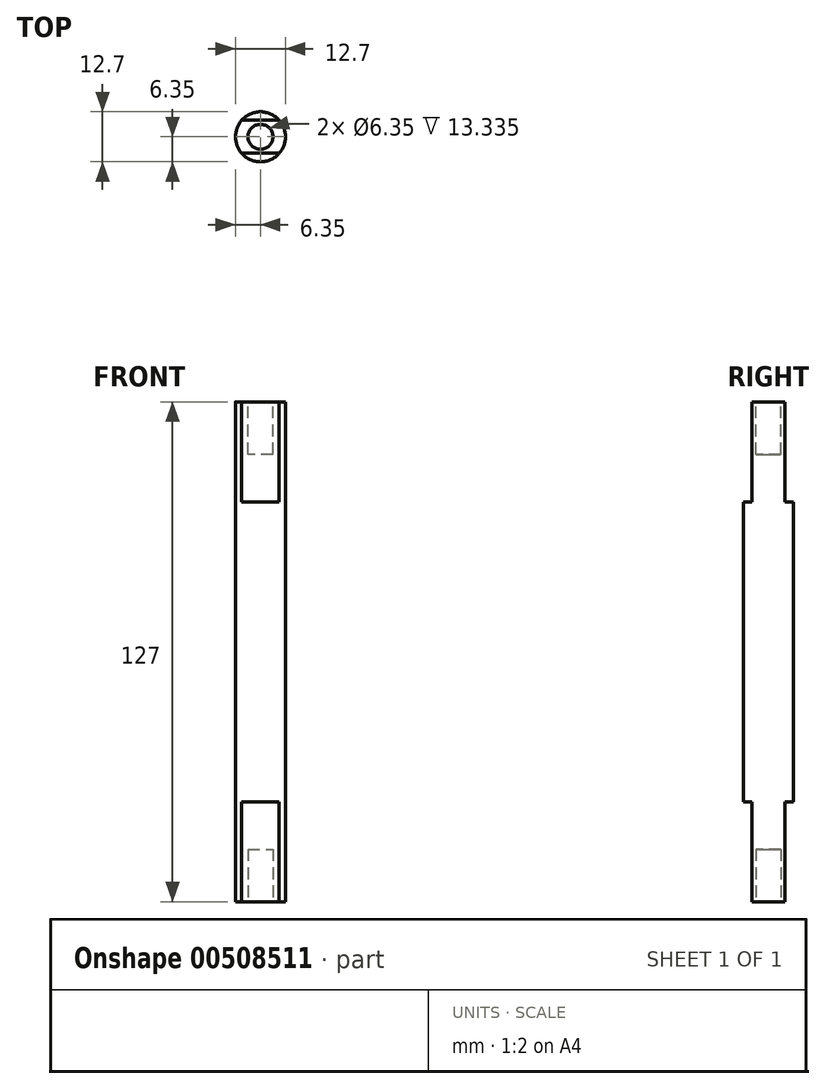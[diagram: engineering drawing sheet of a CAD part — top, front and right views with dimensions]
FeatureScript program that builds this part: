
annotation { "Feature Type Name" : "Feature", "Feature Type Description" : "" }
export const myFeature = defineFeature(function(context is Context, id is Id, definition is map)
    precondition{}
    {
        {
            var Q0;
            Q0=qCreatedBy(makeId("Top.planeOp"),FACE);
            var sketch = newSketch(context, id + "F0", { "sketchPlane" : qUnion([Q0])});
            skCircle(sketch, "E0", {"center": v(0, 0) * mm, "radius": 6.35 * mm});
            skSolve(sketch);
        }
        {
            var Q0;
            Q0=makeQuery(id+"F0.imprint","IMPRINT",FACE,{"disambiguationData":[TD([[makeQuery(id+"F0.imprint","IMPRINT",EDGE,{"derivedFrom":sQuery(id+"F0.wireOp",EDGE,"E0")}),1.0]])]});
            extrude(context, id + "F1", {"entities" : qUnion([Q0]), "depth" : 127 * mm, "offsetDistance" : 25.4 * mm});
        }
        {
            var Q0;
            Q0=makeQuery(id+"F1.opExtrude","CAP_FACE",FACE,{"disambiguationData":[OSD([sQuery(id+"F0.wireOp",EDGE,"E0")])],"isStart":true});
            var sketch = newSketch(context, id + "F2", { "sketchPlane" : qUnion([Q0])});
            skCircle(sketch, "E1", {"center": v(0, 0) * mm, "radius": 3.18 * mm});
            skSolve(sketch);
        }
        {
            var Q0;
            Q0=makeQuery(id+"F2.imprint","IMPRINT",FACE,{"disambiguationData":[TD([[makeQuery(id+"F2.imprint","IMPRINT",EDGE,{"derivedFrom":sQuery(id+"F2.wireOp",EDGE,"E1")}),1.0]])]});
            extrude(context, id + "F3", {"entities" : qUnion([Q0]), "operationType" : NewBodyOperationType.REMOVE, "oppositeDirection" : true, "depth" : 13.33 * mm, "offsetDistance" : 25.4 * mm});
        }
        {
            var Q0;
            Q0=makeQuery(id+"F1.opExtrude","CAP_FACE",FACE,{"disambiguationData":[OSD([sQuery(id+"F0.wireOp",EDGE,"E0")])],"isStart":false});
            var sketch = newSketch(context, id + "F4", { "sketchPlane" : qUnion([Q0])});
            skCircle(sketch, "E2", {"center": v(0, 0) * mm, "radius": 3.18 * mm});
            skSolve(sketch);
        }
        {
            var Q0;
            Q0=makeQuery(id+"F4.imprint","IMPRINT",FACE,{"disambiguationData":[TD([[makeQuery(id+"F4.imprint","IMPRINT",EDGE,{"derivedFrom":sQuery(id+"F4.wireOp",EDGE,"E2")}),1.0]])]});
            extrude(context, id + "F5", {"entities" : qUnion([Q0]), "operationType" : NewBodyOperationType.REMOVE, "oppositeDirection" : true, "depth" : 13.33 * mm, "offsetDistance" : 25.4 * mm});
        }
        {
            var Q0;
            Q0=makeQuery(id+"F1.opExtrude","CAP_FACE",FACE,{"disambiguationData":[OSD([sQuery(id+"F0.wireOp",EDGE,"E0")])],"isStart":true});
            var sketch = newSketch(context, id + "F6", { "sketchPlane" : qUnion([Q0])});
            skLineSegment(sketch, "E3.bottom", {"start": v(4.77, 4.2) * mm, "end": v(-4.77, 4.2) * mm});
            skLineSegment(sketch, "E3.top", {"start": v(4.77, -4.2) * mm, "end": v(-4.77, -4.2) * mm});
            skSolve(sketch);
        }
        {
            var Q0;
            {var subQ0=sQuery(id+"F6.wireOp",EDGE,"E3.bottom");Q0=makeQuery(id+"F6.imprint","IMPRINT",FACE,{"disambiguationData":[TD([[makeQuery(id+"F6.imprint","IMPRINT",EDGE,{"derivedFrom":subQ0}),-1.0]])]});}
            var Q1;
            {var subQ0=sQuery(id+"F6.wireOp",EDGE,"E3.top");Q1=makeQuery(id+"F6.imprint","IMPRINT",FACE,{"disambiguationData":[TD([[makeQuery(id+"F6.imprint","IMPRINT",EDGE,{"derivedFrom":subQ0}),1.0]])]});}
            extrude(context, id + "F7", {"entities" : qUnion([Q0, Q1]), "operationType" : NewBodyOperationType.REMOVE, "oppositeDirection" : true, "depth" : 25.4 * mm, "offsetDistance" : 25.4 * mm});
        }
        {
            var Q0;
            Q0=makeQuery(id+"F1.opExtrude","CAP_FACE",FACE,{"disambiguationData":[OSD([sQuery(id+"F0.wireOp",EDGE,"E0")])],"isStart":false});
            var sketch = newSketch(context, id + "F8", { "sketchPlane" : qUnion([Q0])});
            skLineSegment(sketch, "E4.bottom", {"start": v(-4.77, -4.2) * mm, "end": v(4.77, -4.2) * mm});
            skLineSegment(sketch, "E4.top", {"start": v(-4.77, 4.2) * mm, "end": v(4.77, 4.2) * mm});
            skSolve(sketch);
        }
        {
            var Q0;
            {var subQ0=sQuery(id+"F8.wireOp",EDGE,"E4.bottom");Q0=makeQuery(id+"F8.imprint","IMPRINT",FACE,{"disambiguationData":[TD([[makeQuery(id+"F8.imprint","IMPRINT",EDGE,{"derivedFrom":subQ0}),-1.0]])]});}
            var Q1;
            {var subQ0=sQuery(id+"F8.wireOp",EDGE,"E4.top");Q1=makeQuery(id+"F8.imprint","IMPRINT",FACE,{"disambiguationData":[TD([[makeQuery(id+"F8.imprint","IMPRINT",EDGE,{"derivedFrom":subQ0}),1.0]])]});}
            extrude(context, id + "F9", {"entities" : qUnion([Q0, Q1]), "operationType" : NewBodyOperationType.REMOVE, "oppositeDirection" : true, "depth" : 25.4 * mm, "offsetDistance" : 25.4 * mm});
        }
    });
